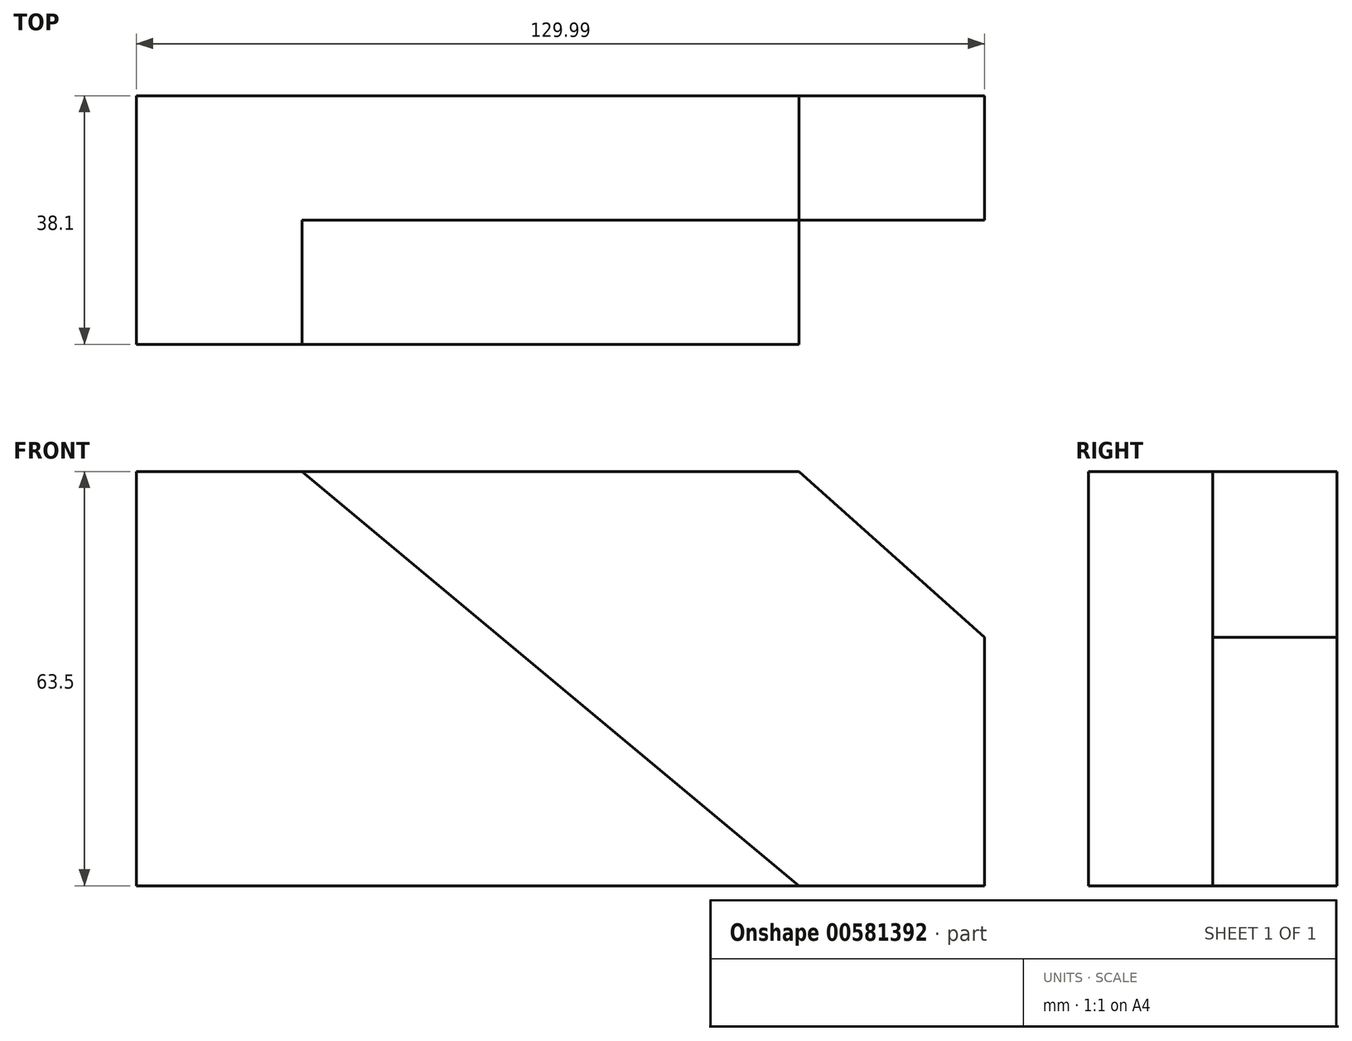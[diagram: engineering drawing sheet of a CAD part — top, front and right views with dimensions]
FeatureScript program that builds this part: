
annotation { "Feature Type Name" : "Feature", "Feature Type Description" : "" }
export const myFeature = defineFeature(function(context is Context, id is Id, definition is map)
    precondition{}
    {
        {
            var Q0;
            Q0=qCreatedBy(makeId("Front.planeOp"),FACE);
            var sketch = newSketch(context, id + "F0", { "sketchPlane" : qUnion([Q0])});
            skLineSegment(sketch, "E0", {"start": v(-57.82, 29.88) * mm, "end": v(-57.82, -33.62) * mm});
            skLineSegment(sketch, "E1", {"start": v(-57.82, -33.62) * mm, "end": v(69.18, -33.62) * mm});
            skLineSegment(sketch, "E2", {"start": v(69.18, -33.62) * mm, "end": v(69.18, 29.88) * mm});
            skLineSegment(sketch, "E3", {"start": v(69.18, 29.88) * mm, "end": v(-57.82, 29.88) * mm});
            skLineSegment(sketch, "E4", {"start": v(-57.82, 29.88) * mm, "end": v(-32.42, 29.88) * mm});
            skLineSegment(sketch, "E5", {"start": v(69.18, -33.62) * mm, "end": v(43.78, -33.62) * mm});
            skLineSegment(sketch, "E6", {"start": v(43.78, -33.62) * mm, "end": v(-32.42, 29.88) * mm});
            skLineSegment(sketch, "E7", {"start": v(69.18, 29.88) * mm, "end": v(43.78, 29.88) * mm});
            skLineSegment(sketch, "E8", {"start": v(69.18, 29.88) * mm, "end": v(69.18, 4.48) * mm});
            skLineSegment(sketch, "E9", {"start": v(43.78, 29.88) * mm, "end": v(69.18, 4.48) * mm});
            skSolve(sketch);
        }
        {
            var Q0;
            Q0=makeQuery(id+"F0.imprint","IMPRINT",FACE,{"disambiguationData":[TD([[makeQuery(id+"F0.imprint","IMPRINT",EDGE,{"derivedFrom":sQuery(id+"F0.wireOp",EDGE,"E0")}),1.0]])]});
            extrude(context, id + "F1", {"entities" : qUnion([Q0]), "depth" : 38.1 * mm, "offsetDistance" : 25.4 * mm});
        }
        {
            var Q0;
            Q0=qCreatedBy(makeId("Front.planeOp"),FACE);
            var sketch = newSketch(context, id + "F2", { "sketchPlane" : qUnion([Q0])});
            skLineSegment(sketch, "E10.bottom", {"start": v(-57.82, -33.62) * mm, "end": v(72.17, -33.62) * mm});
            skLineSegment(sketch, "E10.top", {"start": v(-57.82, 29.88) * mm, "end": v(43.78, 29.88) * mm});
            skLineSegment(sketch, "E10.left", {"start": v(-57.82, -33.62) * mm, "end": v(-57.82, 29.88) * mm});
            skLineSegment(sketch, "E10.right", {"start": v(72.17, -33.62) * mm, "end": v(72.17, 4.48) * mm});
            skLineSegment(sketch, "E11", {"start": v(43.78, 29.88) * mm, "end": v(72.17, 4.48) * mm});
            skSolve(sketch);
        }
        {
            var Q0;
            Q0 = qSketchRegion(id + "F2", true);
            extrude(context, id + "F3", {"entities" : qUnion([Q0]), "operationType" : NewBodyOperationType.ADD, "depth" : 19.05 * mm, "offsetDistance" : 25.4 * mm});
        }
    });
